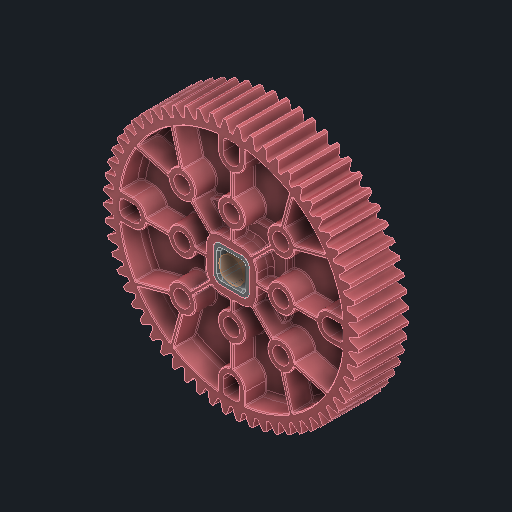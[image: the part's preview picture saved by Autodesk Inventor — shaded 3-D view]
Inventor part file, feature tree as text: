
AUTODESK INVENTOR PART (.ipt)
format: ipt  version: 2024 (Build 280153000, 153)  size: 3,492,352 bytes
history: native  units: in
note: dims shown in document units (in); Inventor stores cm internally (conversion verified against a paired STEP export)
features: other x3, extrude x1
ambient origin geometry x8: Origin, YZ Plane, XZ Plane, XY Plane, X Axis, Y Axis, Z Axis, Center Point
bodies: Solid1 (feature_tree), Solid2 (feature_tree)
feature tree (4):
  other  "Srf1"
  other  "276-7748-001_OVERMOLD Rev3_60T 24DP Gear Rev1_1:1"
  other  "276-7573-002 Rev7_2:1"
  extrude  "ExtrusionSrf1"  Depth=0.25in
